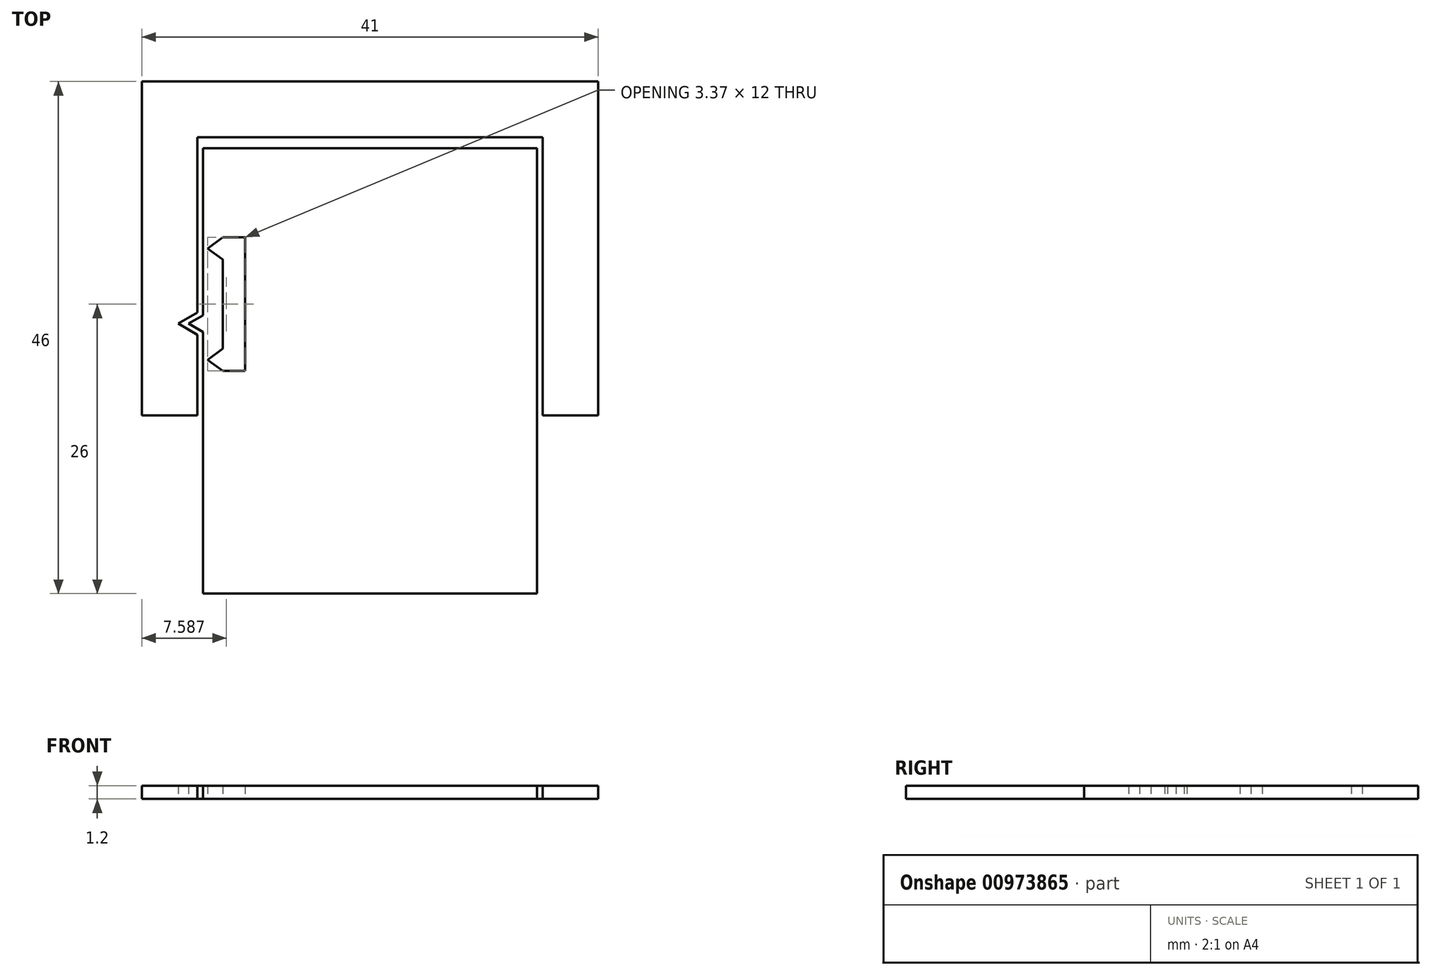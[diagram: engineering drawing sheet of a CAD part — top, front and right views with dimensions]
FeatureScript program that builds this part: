
annotation { "Feature Type Name" : "Feature", "Feature Type Description" : "" }
export const myFeature = defineFeature(function(context is Context, id is Id, definition is map)
    precondition{}
    {
        {
            var Q0;
            Q0=qCreatedBy(makeId("Top.planeOp"),FACE);
            var sketch = newSketch(context, id + "F0", { "sketchPlane" : qUnion([Q0])});
            skLineSegment(sketch, "E0.bottom", {"start": v(15, 20) * mm, "end": v(-15, 20) * mm});
            skLineSegment(sketch, "E0.top", {"start": v(15, -20) * mm, "end": v(-15, -20) * mm});
            skLineSegment(sketch, "E0.left", {"start": v(15, 20) * mm, "end": v(15, -20) * mm});
            skPoint(sketch, "E0.middle", {"position": v(0, 0) * mm});
            skLineSegment(sketch, "E1.bottom", {"start": v(-15.5, -4) * mm, "end": v(-20.5, -4) * mm});
            skLineSegment(sketch, "E1.top", {"start": v(-15.5, 26) * mm, "end": v(-20.5, 26) * mm});
            skLineSegment(sketch, "E1.right", {"start": v(-20.5, -4) * mm, "end": v(-20.5, 26) * mm});
            skLineSegment(sketch, "E2.bottom", {"start": v(-15.5, 26) * mm, "end": v(20.5, 26) * mm});
            skLineSegment(sketch, "E2.top", {"start": v(-15.5, 21) * mm, "end": v(20.5, 21) * mm});
            skLineSegment(sketch, "E2.left", {"start": v(-15.5, 26) * mm, "end": v(-15.5, 21) * mm});
            skLineSegment(sketch, "E2.right", {"start": v(20.5, 26) * mm, "end": v(20.5, 21) * mm});
            skLineSegment(sketch, "E3.bottom", {"start": v(20.5, 21) * mm, "end": v(15.5, 21) * mm});
            skLineSegment(sketch, "E3.top", {"start": v(20.5, -4) * mm, "end": v(15.5, -4) * mm});
            skLineSegment(sketch, "E3.left", {"start": v(20.5, 21) * mm, "end": v(20.5, -4) * mm});
            skLineSegment(sketch, "E3.right", {"start": v(15.5, 21) * mm, "end": v(15.5, -4) * mm});
            skLineSegment(sketch, "E4.bottom", {"start": v(-13.23, 12) * mm, "end": v(-11.23, 12) * mm});
            skLineSegment(sketch, "E4.top", {"start": v(-13.23, 0) * mm, "end": v(-11.23, 0) * mm});
            skLineSegment(sketch, "E4.right", {"start": v(-11.23, 12) * mm, "end": v(-11.23, 0) * mm});
            skLineSegment(sketch, "E5", {"start": v(-13.23, 10) * mm, "end": v(-14.6, 11) * mm});
            skLineSegment(sketch, "E6", {"start": v(-14.6, 11) * mm, "end": v(-13.23, 12) * mm});
            skLineSegment(sketch, "E7", {"start": v(-13.23, 0) * mm, "end": v(-14.6, 1) * mm});
            skLineSegment(sketch, "E8", {"start": v(-14.6, 1) * mm, "end": v(-13.23, 2) * mm});
            skLineSegment(sketch, "E9", {"start": v(-13.23, 10) * mm, "end": v(-13.23, 2) * mm});
            skLineSegment(sketch, "E10", {"start": v(-15, 3.5) * mm, "end": v(-16.3, 4.25) * mm});
            skLineSegment(sketch, "E11", {"start": v(-16.3, 4.25) * mm, "end": v(-15, 5) * mm});
            skLineSegment(sketch, "E12", {"start": v(-15.5, 5.25) * mm, "end": v(-17.23, 4.25) * mm});
            skLineSegment(sketch, "E13", {"start": v(-17.23, 4.25) * mm, "end": v(-15.5, 3.25) * mm});
            skLineSegment(sketch, "E14", {"start": v(-15.5, -4) * mm, "end": v(-15.5, 3.25) * mm});
            skLineSegment(sketch, "E15", {"start": v(-15.5, 5.25) * mm, "end": v(-15.5, 21) * mm});
            skLineSegment(sketch, "E16", {"start": v(-15, 3.5) * mm, "end": v(-15, -20) * mm});
            skLineSegment(sketch, "E17", {"start": v(-15, 5) * mm, "end": v(-15, 20) * mm});
            skSolve(sketch);
        }
        {
            var Q0;
            Q0=makeQuery(id+"F0.imprint","IMPRINT",FACE,{"disambiguationData":[TD([[makeQuery(id+"F0.imprint","IMPRINT",EDGE,{"derivedFrom":sQuery(id+"F0.wireOp",EDGE,"E0.bottom")}),1.0]])]});
            var Q1;
            Q1=makeQuery(id+"F0.imprint","IMPRINT",FACE,{"disambiguationData":[TD([[makeQuery(id+"F0.imprint","IMPRINT",EDGE,{"derivedFrom":sQuery(id+"F0.wireOp",EDGE,"E1.bottom")}),-1.0]])]});
            var Q2;
            Q2=makeQuery(id+"F0.imprint","IMPRINT",FACE,{"disambiguationData":[TD([[makeQuery(id+"F0.imprint","IMPRINT",EDGE,{"derivedFrom":sQuery(id+"F0.wireOp",EDGE,"E2.bottom")}),-1.0]])]});
            var Q3;
            Q3=makeQuery(id+"F0.imprint","IMPRINT",FACE,{"disambiguationData":[TD([[makeQuery(id+"F0.imprint","IMPRINT",EDGE,{"derivedFrom":sQuery(id+"F0.wireOp",EDGE,"E3.top")}),-1.0]])]});
            extrude(context, id + "F1", {"entities" : qUnion([Q0, Q1, Q2, Q3]), "depth" : 1.2 * mm, "offsetDistance" : 25 * mm});
        }
    });
